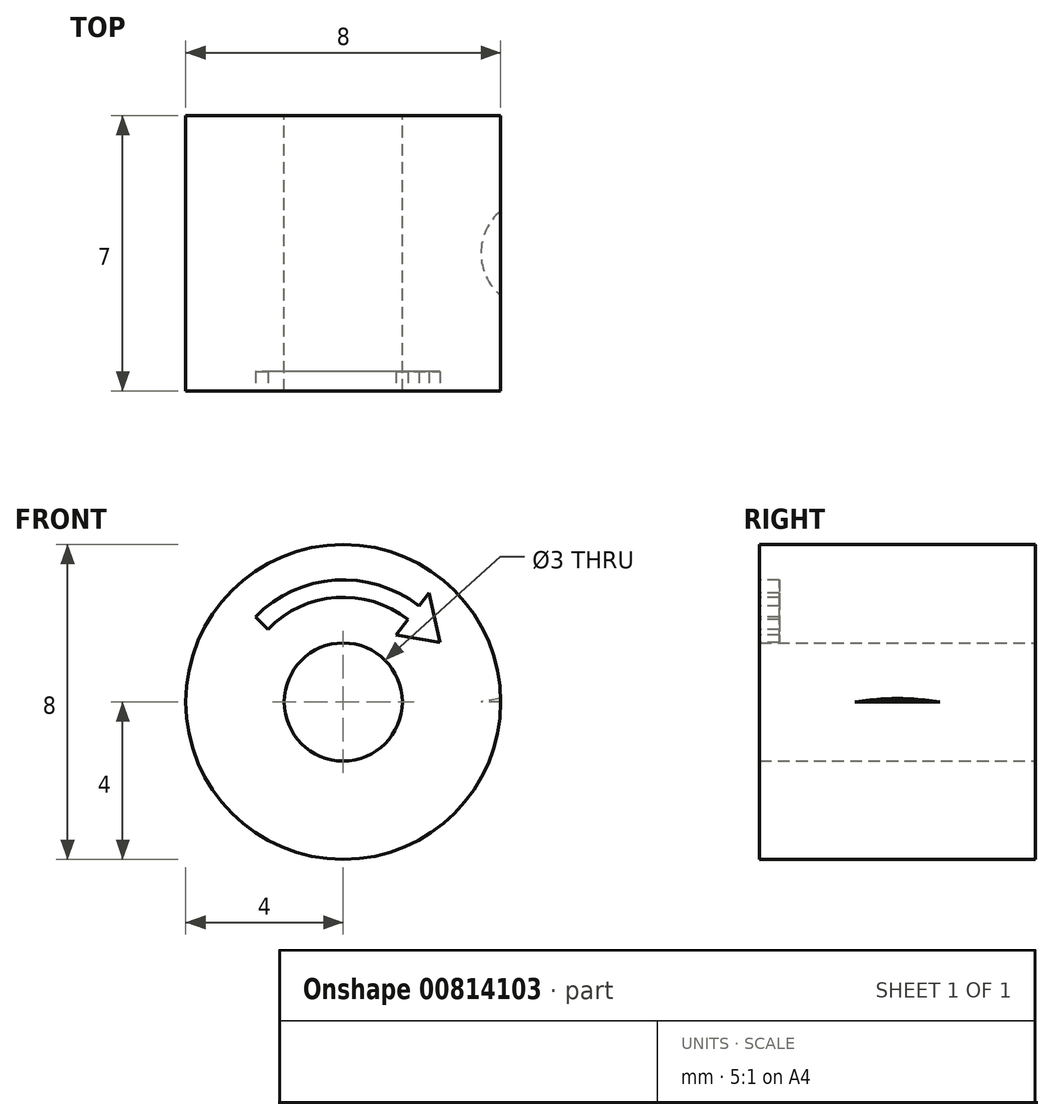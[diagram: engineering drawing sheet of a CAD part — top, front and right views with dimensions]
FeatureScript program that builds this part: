
annotation { "Feature Type Name" : "Feature", "Feature Type Description" : "" }
export const myFeature = defineFeature(function(context is Context, id is Id, definition is map)
    precondition{}
    {
        {
            var Q0;
            Q0=qCreatedBy(makeId("Front.planeOp"),FACE);
            var sketch = newSketch(context, id + "F0", { "sketchPlane" : qUnion([Q0])});
            skCircle(sketch, "E0", {"center": v(0, 0) * mm, "radius": 4 * mm});
            skCircle(sketch, "E1", {"center": v(0, 0) * mm, "radius": 1.5 * mm});
            skSolve(sketch);
        }
        {
            var Q0;
            Q0 = qSketchRegion(id + "F0", true);
            extrude(context, id + "F1", {"entities" : qUnion([Q0]), "depth" : 7 * mm, "offsetDistance" : 25 * mm});
        }
        {
            var Q0;
            Q0=makeQuery(id+"F1.opExtrude","CAP_FACE",FACE,{"disambiguationData":[OSD([sQuery(id+"F0.wireOp",EDGE,"E0"),sQuery(id+"F0.wireOp",EDGE,"E1")])],"isStart":false});
            cPlane(context, id + "F2", {"entities" : qUnion([Q0]), "cplaneType" : CPlaneType.OFFSET, "offset" : 3.5 * mm, "oppositeDirection" : true, "width" : 150 * mm, "height" : 150 * mm});
        }
        {
            var Q0;
            Q0=qCreatedBy(id+"F2.planeOp",FACE);
            var sketch = newSketch(context, id + "F3", { "sketchPlane" : qUnion([Q0])});
            skLineSegment(sketch, "E2", {"start": v(4.9, 0) * mm, "end": v(3.5, 0) * mm});
            skLineSegment(sketch, "E3", {"start": v(3.5, 0) * mm, "end": v(4.9, 0.25) * mm});
            skLineSegment(sketch, "E4", {"start": v(4.9, 0.25) * mm, "end": v(4.9, 0) * mm});
            skSolve(sketch);
        }
        {
            var Q0;
            Q0 = qSketchRegion(id + "F3", true);
            var Q1;
            Q1=sQuery(id+"F3.wireOp",EDGE,"E4");
            revolve(context, id + "F4", {"operationType" : NewBodyOperationType.REMOVE, "surfaceOperationType" : NewSurfaceOperationType.NEW, "entities" : qUnion([Q0]), "axis" : qUnion([Q1]), "revolveType" : RevolveType.FULL, "oppositeDirection" : true});
        }
        {
            var Q0;
            Q0=makeQuery(id+"F1.opExtrude","CAP_FACE",FACE,{"disambiguationData":[OSD([sQuery(id+"F0.wireOp",EDGE,"E0"),sQuery(id+"F0.wireOp",EDGE,"E1")])],"isStart":false});
            var sketch = newSketch(context, id + "F5", { "sketchPlane" : qUnion([Q0])});
            skArc(sketch, "E5", {"start": v(-2.23, 2.15) * mm, "mid": v(-0.21, 3.1) * mm, "end": v(1.92, 2.44) * mm});
            skArc(sketch, "E6", {"start": v(-1.92, 1.85) * mm, "mid": v(-0.18, 2.65) * mm, "end": v(1.65, 2.1) * mm});
            skLineSegment(sketch, "E7", {"start": v(-2.23, 2.15) * mm, "end": v(-1.92, 1.85) * mm});
            skLineSegment(sketch, "E8", {"start": v(2.18, 2.77) * mm, "end": v(1.34, 1.7) * mm});
            skLineSegment(sketch, "E9", {"start": v(1.34, 1.7) * mm, "end": v(2.45, 1.51) * mm});
            skLineSegment(sketch, "E10", {"start": v(2.45, 1.51) * mm, "end": v(2.18, 2.77) * mm});
            skSolve(sketch);
        }
        {
            var Q0;
            Q0 = qSketchRegion(id + "F5", true);
            extrude(context, id + "F6", {"entities" : qUnion([Q0]), "operationType" : NewBodyOperationType.REMOVE, "oppositeDirection" : true, "depth" : 0.5 * mm, "offsetDistance" : 25 * mm});
        }
    });
